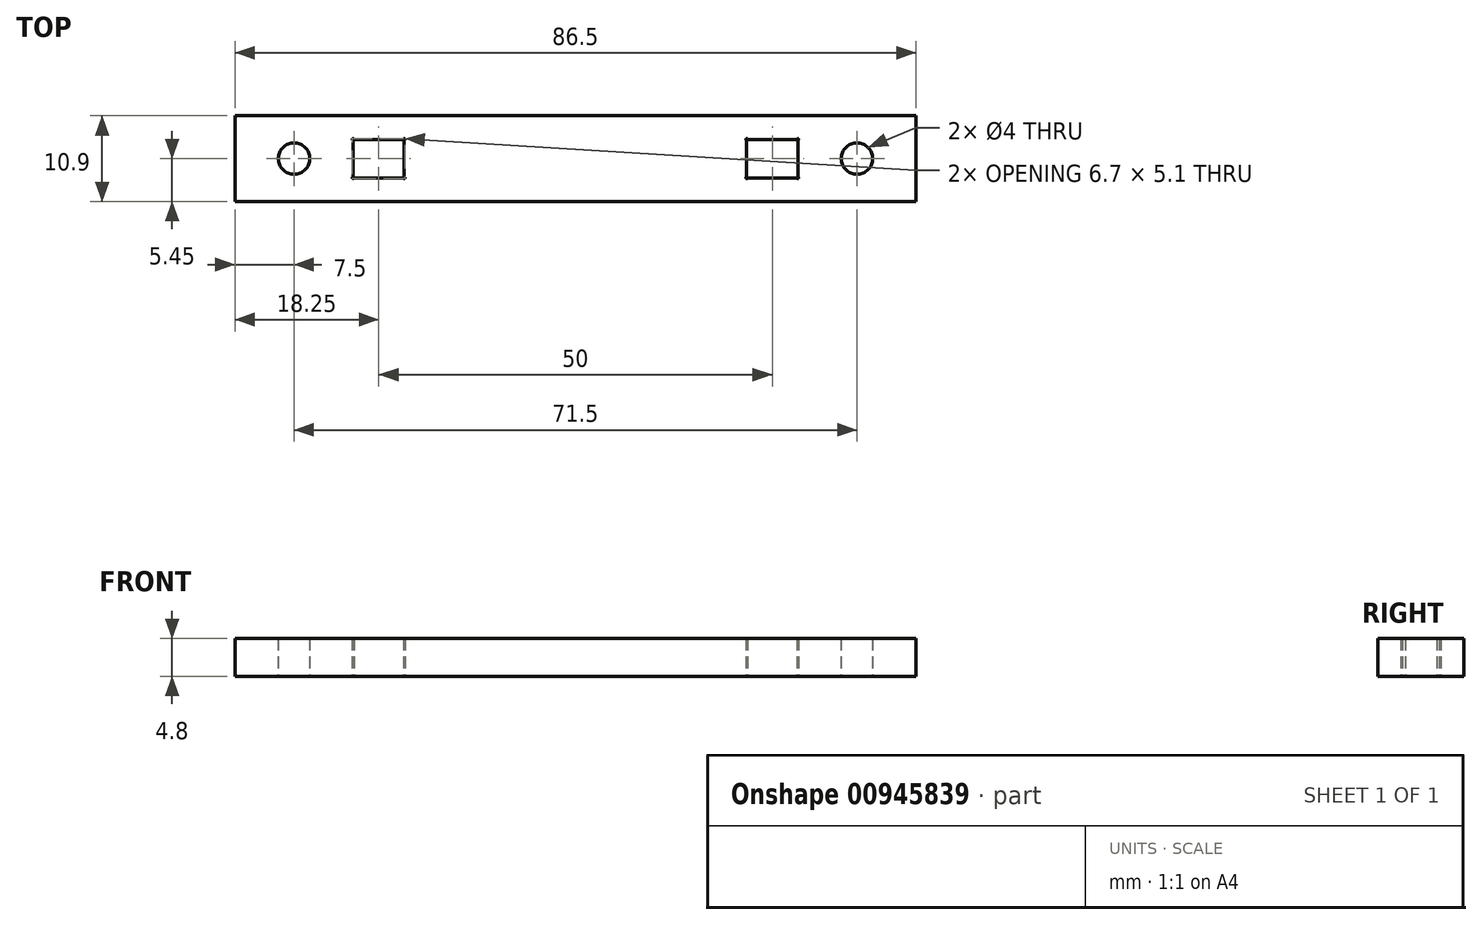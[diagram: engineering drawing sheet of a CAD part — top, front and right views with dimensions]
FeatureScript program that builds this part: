
annotation { "Feature Type Name" : "Feature", "Feature Type Description" : "" }
export const myFeature = defineFeature(function(context is Context, id is Id, definition is map)
    precondition{}
    {
        {
            assignVariable(context, id + "F0", {"name" : "QRDHeight", "anyValue" : 4.8});
        }
        {
            var Q0;
            Q0=qCreatedBy(makeId("Top.planeOp"),FACE);
            var sketch = newSketch(context, id + "F1", { "sketchPlane" : qUnion([Q0])});
            skLineSegment(sketch, "E0", {"start": v(0, 0) * mm, "end": v(0, 5.45) * mm, "construction": true});
            skLineSegment(sketch, "E1", {"start": v(0, 0) * mm, "end": v(-43.25, 0) * mm, "construction": true});
            skLineSegment(sketch, "E2", {"start": v(-43.25, 0) * mm, "end": v(-43.25, 5.45) * mm});
            skLineSegment(sketch, "E3", {"start": v(-43.25, 5.45) * mm, "end": v(0, 5.45) * mm});
            skLineSegment(sketch, "E4.MirrorCS", {"start": v(-43.25, -5.45) * mm, "end": v(0, -5.45) * mm});
            skLineSegment(sketch, "E5.MirrorCS", {"start": v(-43.25, 0) * mm, "end": v(-43.25, -5.45) * mm});
            skLineSegment(sketch, "E6.MirrorCS", {"start": v(43.25, 5.45) * mm, "end": v(0, 5.45) * mm});
            skLineSegment(sketch, "E7.MirrorCS", {"start": v(43.25, 0) * mm, "end": v(43.25, 5.45) * mm});
            skLineSegment(sketch, "E8.MirrorCS", {"start": v(43.25, 0) * mm, "end": v(43.25, -5.45) * mm});
            skLineSegment(sketch, "E9.MirrorCS", {"start": v(43.25, -5.45) * mm, "end": v(0, -5.45) * mm});
            skLineSegment(sketch, "E10", {"start": v(0, 0) * mm, "end": v(25, 0) * mm, "construction": true});
            skLineSegment(sketch, "E11.bottom", {"start": v(28.25, -2.45) * mm, "end": v(21.75, -2.45) * mm});
            skLineSegment(sketch, "E11.top", {"start": v(28.25, 2.45) * mm, "end": v(21.75, 2.45) * mm});
            skLineSegment(sketch, "E11.left", {"start": v(28.25, -2.45) * mm, "end": v(28.25, 2.45) * mm});
            skLineSegment(sketch, "E11.right", {"start": v(21.75, -2.45) * mm, "end": v(21.75, 2.45) * mm});
            skPoint(sketch, "E11.middle", {"position": v(25, 0) * mm});
            skLineSegment(sketch, "E12", {"start": v(28.25, 0) * mm, "end": v(35.75, 0) * mm, "construction": true});
            skCircle(sketch, "E13", {"center": v(35.75, 0) * mm, "radius": 2 * mm});
            skLineSegment(sketch, "E14.MirrorCS", {"start": v(-21.75, -2.45) * mm, "end": v(-21.75, 2.45) * mm});
            skLineSegment(sketch, "E15.MirrorCS", {"start": v(-28.25, 2.45) * mm, "end": v(-21.75, 2.45) * mm});
            skLineSegment(sketch, "E16.MirrorCS", {"start": v(-28.25, -2.45) * mm, "end": v(-21.75, -2.45) * mm});
            skLineSegment(sketch, "E17.MirrorCS", {"start": v(-28.25, -2.45) * mm, "end": v(-28.25, 2.45) * mm});
            skCircle(sketch, "E18.MirrorC", {"center": v(-35.75, 0) * mm, "radius": 2 * mm});
            skCircle(sketch, "E19", {"center": v(21.75, 2.45) * mm, "radius": 0.1 * mm});
            skCircle(sketch, "E20", {"center": v(28.25, 2.45) * mm, "radius": 0.1 * mm});
            skCircle(sketch, "E21", {"center": v(28.25, -2.45) * mm, "radius": 0.1 * mm});
            skCircle(sketch, "E22", {"center": v(21.75, -2.45) * mm, "radius": 0.1 * mm});
            skCircle(sketch, "E23.MirrorC", {"center": v(-21.75, 2.45) * mm, "radius": 0.1 * mm});
            skCircle(sketch, "E24.MirrorC", {"center": v(-21.75, -2.45) * mm, "radius": 0.1 * mm});
            skCircle(sketch, "E25.MirrorC", {"center": v(-28.25, -2.45) * mm, "radius": 0.1 * mm});
            skCircle(sketch, "E26.MirrorC", {"center": v(-28.25, 2.45) * mm, "radius": 0.1 * mm});
            skSolve(sketch);
        }
        {
            var Q0;
            Q0 = qSketchRegion(id + "F1", true);
            extrude(context, id + "F2", {"entities" : qUnion([Q0]), "depth" : (getVariable(context, 'QRDHeight')) * mm, "offsetDistance" : 25 * mm});
        }
    });
